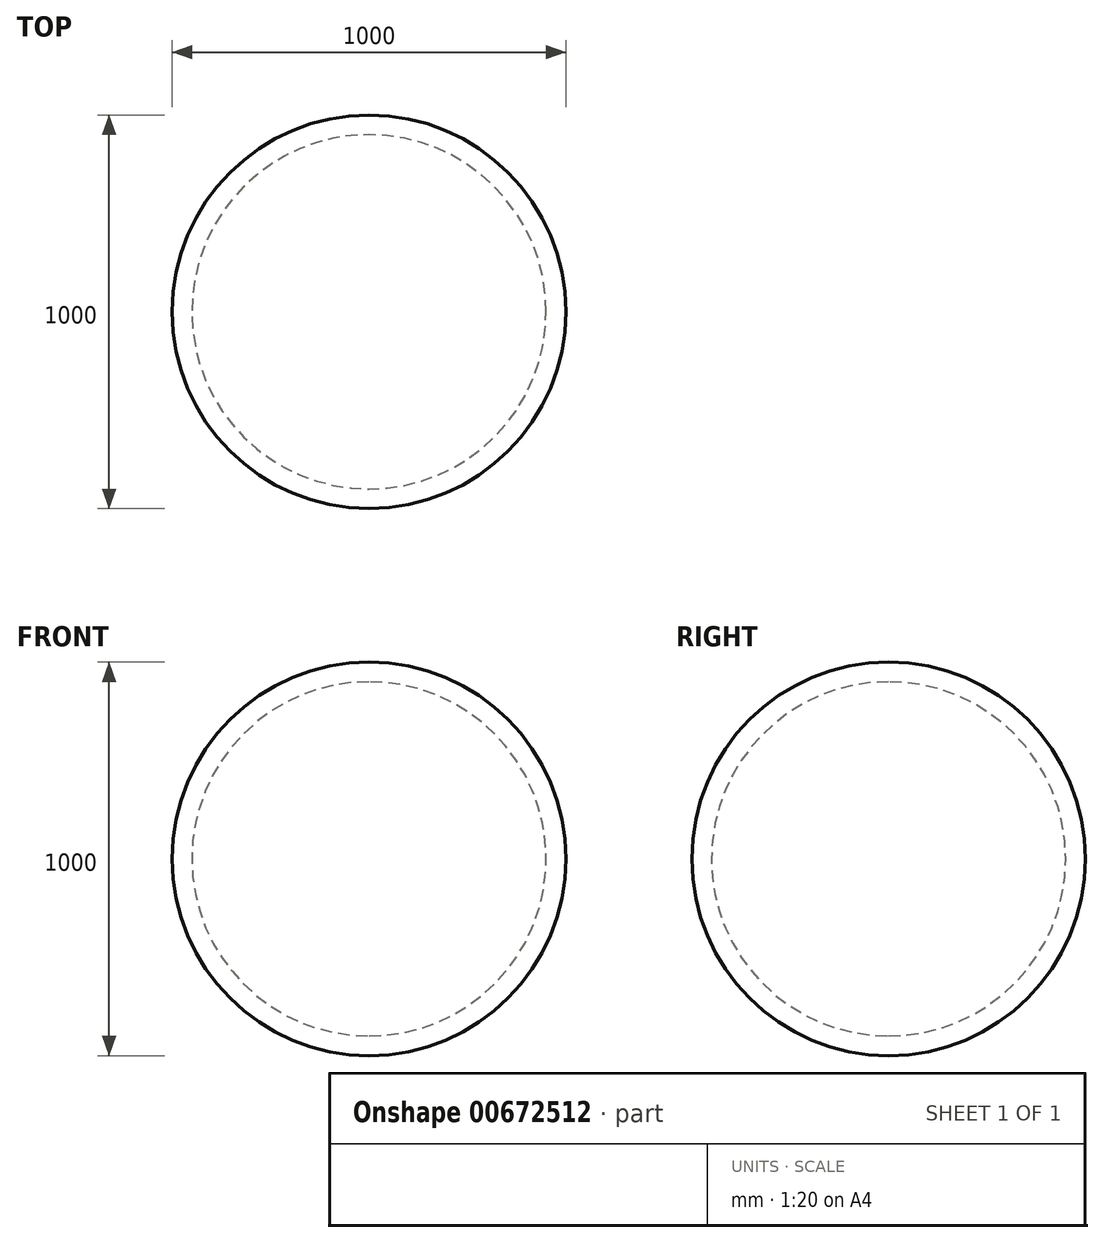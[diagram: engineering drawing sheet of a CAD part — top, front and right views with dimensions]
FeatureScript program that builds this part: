
annotation { "Feature Type Name" : "Feature", "Feature Type Description" : "" }
export const myFeature = defineFeature(function(context is Context, id is Id, definition is map)
    precondition{}
    {
        {
            var Q0;
            Q0=qCreatedBy(makeId("Front.planeOp"),FACE);
            var sketch = newSketch(context, id + "F0", { "sketchPlane" : qUnion([Q0])});
            skArc(sketch, "E0", {"start": v(0, -500) * mm, "mid": v(500, 0) * mm, "end": v(0, 500) * mm});
            skLineSegment(sketch, "E1", {"start": v(0, 500) * mm, "end": v(0, -500) * mm});
            skSolve(sketch);
        }
        {
            var Q0;
            Q0 = qSketchRegion(id + "F0", true);
            var Q1;
            Q1=sQuery(id+"F0.wireOp",EDGE,"E1");
            revolve(context, id + "F1", {"entities" : qUnion([Q0]), "axis" : qUnion([Q1]), "revolveType" : RevolveType.FULL});
        }
        {
            var Q0;
            Q0=qCreatedBy(makeId("Front.planeOp"),FACE);
            var sketch = newSketch(context, id + "F2", { "sketchPlane" : qUnion([Q0])});
            skArc(sketch, "E2", {"start": v(0, -450) * mm, "mid": v(450, 0) * mm, "end": v(0, 450) * mm});
            skLineSegment(sketch, "E3", {"start": v(0, 450) * mm, "end": v(0, -450) * mm});
            skSolve(sketch);
        }
        {
            var Q0;
            Q0 = qSketchRegion(id + "F2", true);
            var Q1;
            Q1=sQuery(id+"F2.wireOp",EDGE,"E3");
            revolve(context, id + "F3", {"operationType" : NewBodyOperationType.REMOVE, "entities" : qUnion([Q0]), "axis" : qUnion([Q1]), "revolveType" : RevolveType.FULL, "oppositeDirection" : true});
        }
    });
